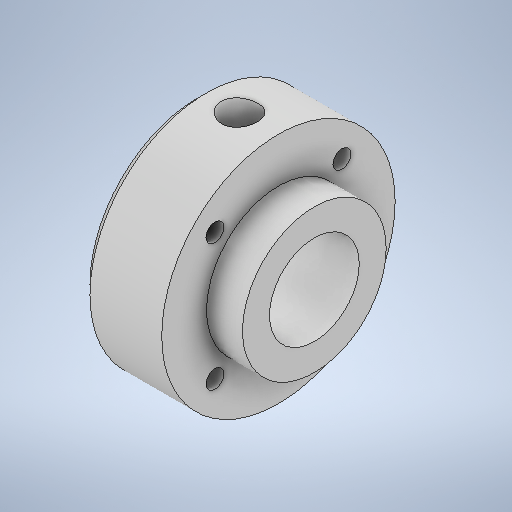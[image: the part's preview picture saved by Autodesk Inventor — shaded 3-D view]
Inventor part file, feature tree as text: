
AUTODESK INVENTOR PART (.ipt)
format: ipt  version: 2025.1 (Build 291241000, 241)  size: 307,712 bytes
history: native  units: mm
features: sketch x5, hole x2, plane x2, revolve x1, pattern_circular x1, chamfer x1, sweep x1
ambient origin geometry x8: Origin, YZ Plane, XZ Plane, XY Plane, X Axis, Y Axis, Z Axis, Center Point
bodies: Solid1 (feature_tree)
feature tree (13):
  revolve  "Revolution1"  [1 undecoded]
  hole  "Hole1"  [1 undecoded]
  pattern_circular  "Circular Pattern1"  Count=2  [1 undecoded]
  hole  "Hole2"  [1 undecoded]
  chamfer  "Chamfer1"  Distance=2.0mm Angle=45.0deg
  plane  "Work Plane1"
  sketch  "Sketch4"  dims[d5=45.0deg d6=20.0mm]
  plane  "Work Plane2"
  sweep  "Sweep1"
  sketch  "Sketch1"  dims[d0=16.0mm d1=9.0mm]
  sketch  "Sketch2"  dims[d2=4.0mm d3=26.0mm]
  sketch  "Sketch3"  dims[d4=90.0deg]
  sketch  "Sketch5"  dims[d7=2.0mm d8=6.0mm d9=4.0mm d10=2.0mm d11=90.0deg d12=8.0mm d13=0.0mm d14=40.0mm d15=360.0deg d17=10.0mm d18=6.0mm d19=4.0mm d20=2.0mm d21=90.0deg d22=8.0mm d23=0.0mm d24=1.0mm d25=2.0mm d26=45.0deg d27=0.0mm d28=3.490659mm d29=2.0mm d30=12.5mm d31=4.0mm d32=0.0mm d33=0.0mm d34=2.0mm]
note: 4 required parameter values undecoded (feature->parameter linkage not recoverable at this tier; creation-order binding heuristic only, values carry confidence <= 0.55)